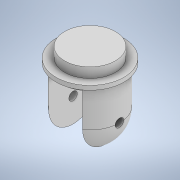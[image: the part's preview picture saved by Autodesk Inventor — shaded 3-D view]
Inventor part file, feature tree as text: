
AUTODESK INVENTOR PART (.ipt)
format: ipt  version: 2020 (Build 240168000, 168)  size: 159,744 bytes
history: native  units: in
note: dims shown in document units (in); Inventor stores cm internally (conversion verified against a paired STEP export)
features: extrude x2, sketch x2, revolve x1
ambient origin geometry x8: Origin, YZ Plane, XZ Plane, XY Plane, X Axis, Y Axis, Z Axis, Center Point
bodies: Solid1 (feature_tree)
feature tree (5):
  revolve  "Revolution1"  Angle=90.0deg
  extrude  "Extrusion2"  Depth=0.25in
  extrude  "Extrusion3"  Depth=1.75in TaperAngle=0.0deg
  sketch  "Sketch3"  dims[d0=3.5in d2=90.0deg]
  sketch  "Sketch4"  dims[d7=2.205in d9=2.0in d11=1.75in d12=0.0in d14=0.5in d15=1.75in d16=0.0in d17=2.0in d18=1.5in d19=0.25in d20=2.0in]
